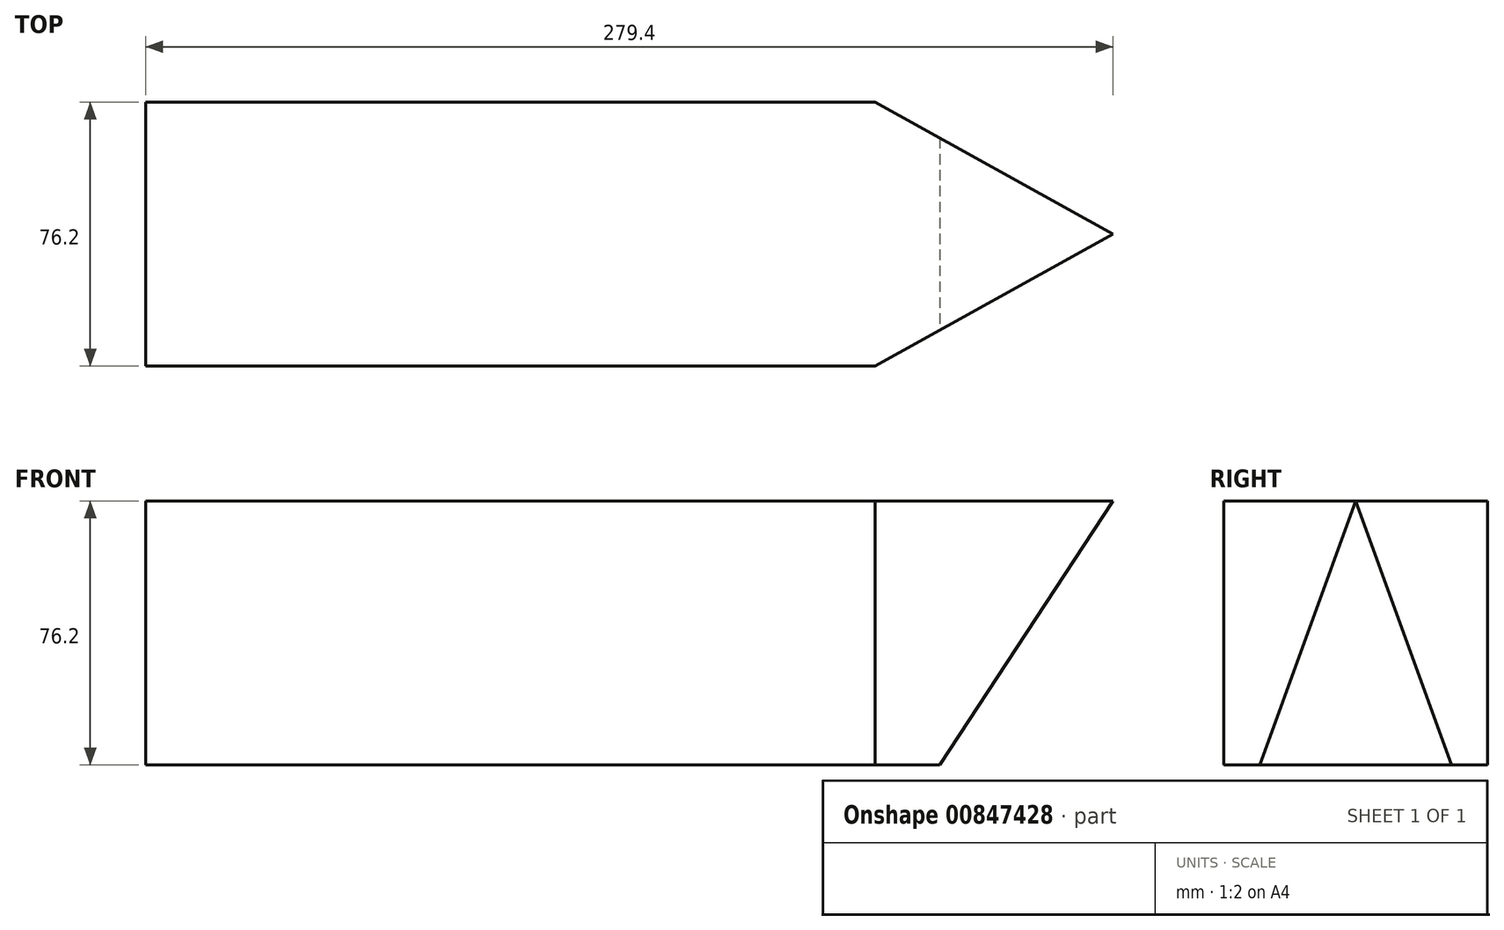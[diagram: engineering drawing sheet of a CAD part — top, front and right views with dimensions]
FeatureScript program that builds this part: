
annotation { "Feature Type Name" : "Feature", "Feature Type Description" : "" }
export const myFeature = defineFeature(function(context is Context, id is Id, definition is map)
    precondition{}
    {
        {
            var Q0;
            Q0=qCreatedBy(makeId("Top.planeOp"),FACE);
            var sketch = newSketch(context, id + "F0", { "sketchPlane" : qUnion([Q0])});
            skLineSegment(sketch, "E0.bottom", {"start": v(-151.63, -10.53) * mm, "end": v(127.77, -10.53) * mm});
            skLineSegment(sketch, "E0.top", {"start": v(-151.63, -86.73) * mm, "end": v(127.77, -86.73) * mm});
            skLineSegment(sketch, "E0.left", {"start": v(-151.63, -10.53) * mm, "end": v(-151.63, -86.73) * mm});
            skLineSegment(sketch, "E0.right", {"start": v(127.77, -10.53) * mm, "end": v(127.77, -86.73) * mm});
            skSolve(sketch);
        }
        {
            var Q0;
            Q0 = qSketchRegion(id + "F0", true);
            extrude(context, id + "F1", {"entities" : qUnion([Q0]), "depth" : 76.2 * mm, "offsetDistance" : 25.4 * mm});
        }
        {
            var Q0;
            Q0=makeQuery(id+"F1.opExtrude","SWEPT_FACE",FACE,{"disambiguationData":[OSD([sQuery(id+"F0.wireOp",EDGE,"E0.top")])]});
            var sketch = newSketch(context, id + "F2", { "sketchPlane" : qUnion([Q0])});
            skLineSegment(sketch, "E1", {"start": v(127.77, 76.2) * mm, "end": v(77.79, 0) * mm});
            skLineSegment(sketch, "E2", {"start": v(77.79, 0) * mm, "end": v(127.77, 0) * mm});
            skLineSegment(sketch, "E3", {"start": v(127.77, 0) * mm, "end": v(127.77, 76.2) * mm});
            skSolve(sketch);
        }
        {
            var Q0;
            Q0 = qSketchRegion(id + "F2", true);
            extrude(context, id + "F3", {"entities" : qUnion([Q0]), "operationType" : NewBodyOperationType.REMOVE, "endBound" : BoundingType.THROUGH_ALL, "oppositeDirection" : true, "depth" : 25.4 * mm, "offsetDistance" : 25.4 * mm});
        }
        {
            var Q0;
            Q0=makeQuery(id+"F1.opExtrude","CAP_FACE",FACE,{"disambiguationData":[OSD([sQuery(id+"F0.wireOp",EDGE,"E0.bottom"),sQuery(id+"F0.wireOp",EDGE,"E0.top"),sQuery(id+"F0.wireOp",EDGE,"E0.left"),sQuery(id+"F0.wireOp",EDGE,"E0.right")])],"isStart":false});
            var sketch = newSketch(context, id + "F4", { "sketchPlane" : qUnion([Q0])});
            skLineSegment(sketch, "E4", {"start": v(59.05, -86.73) * mm, "end": v(127.77, -48.63) * mm});
            skLineSegment(sketch, "E5", {"start": v(127.77, -48.63) * mm, "end": v(59.05, -10.53) * mm});
            skLineSegment(sketch, "E6", {"start": v(59.05, -86.73) * mm, "end": v(127.77, -86.73) * mm});
            skLineSegment(sketch, "E7", {"start": v(127.77, -86.73) * mm, "end": v(127.77, -10.53) * mm});
            skLineSegment(sketch, "E8", {"start": v(127.77, -10.53) * mm, "end": v(59.05, -10.53) * mm});
            skSolve(sketch);
        }
        {
            var Q0;
            Q0 = qSketchRegion(id + "F4", true);
            extrude(context, id + "F5", {"entities" : qUnion([Q0]), "operationType" : NewBodyOperationType.REMOVE, "endBound" : BoundingType.THROUGH_ALL, "oppositeDirection" : true, "depth" : 105.16 * mm, "offsetDistance" : 25.4 * mm});
        }
    });
